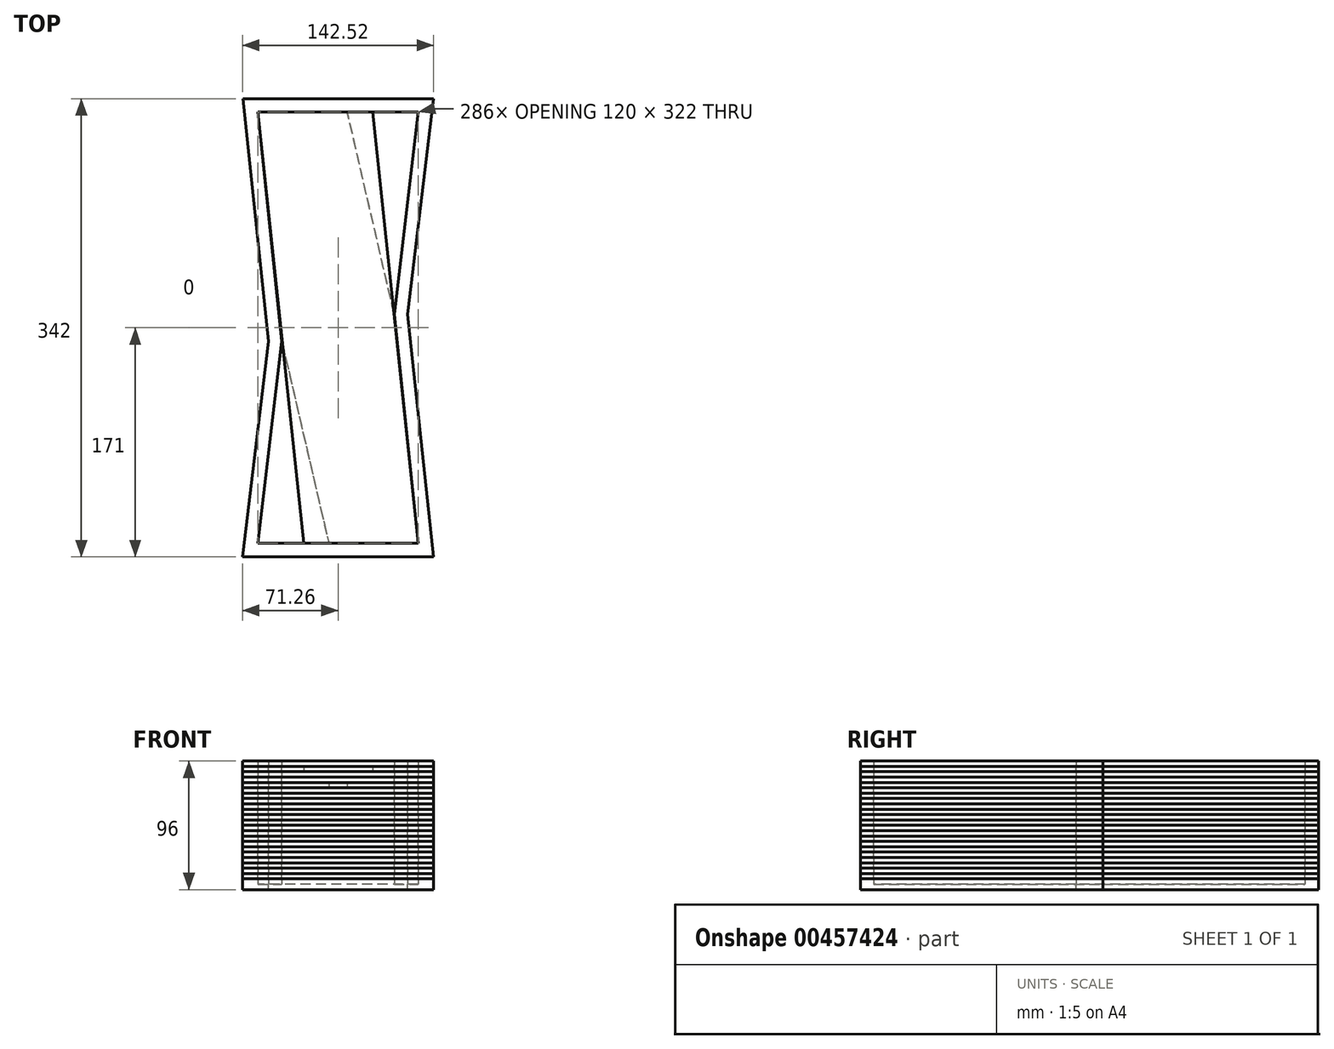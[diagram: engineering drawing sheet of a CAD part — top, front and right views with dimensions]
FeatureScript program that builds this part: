
annotation { "Feature Type Name" : "Feature", "Feature Type Description" : "" }
export const myFeature = defineFeature(function(context is Context, id is Id, definition is map)
    precondition{}
    {
        {
            var Q0;
            Q0=qCreatedBy(makeId("Top.planeOp"),FACE);
            var sketch = newSketch(context, id + "F0", { "sketchPlane" : qUnion([Q0])});
            skLineSegment(sketch, "E0", {"start": v(-71.26, -171) * mm, "end": v(-52.06, -9.93) * mm});
            skLineSegment(sketch, "E1", {"start": v(-52.06, -9.93) * mm, "end": v(-71.1, 171) * mm});
            skLineSegment(sketch, "E2", {"start": v(-71.1, 171) * mm, "end": v(71.26, 171) * mm});
            skLineSegment(sketch, "E3", {"start": v(71.26, 171) * mm, "end": v(52.06, 9.93) * mm});
            skLineSegment(sketch, "E4", {"start": v(52.06, 9.93) * mm, "end": v(71.1, -171) * mm});
            skLineSegment(sketch, "E5", {"start": v(71.1, -171) * mm, "end": v(-71.26, -171) * mm});
            skLineSegment(sketch, "E6", {"start": v(-60, 161) * mm, "end": v(-42, -10) * mm});
            skLineSegment(sketch, "E7", {"start": v(-42, -10) * mm, "end": v(-60, -161) * mm});
            skLineSegment(sketch, "E8", {"start": v(-60, -161) * mm, "end": v(60, -161) * mm});
            skLineSegment(sketch, "E9", {"start": v(60, -161) * mm, "end": v(42, 10) * mm});
            skLineSegment(sketch, "E10", {"start": v(42, 10) * mm, "end": v(60, 161) * mm});
            skLineSegment(sketch, "E11", {"start": v(60, 161) * mm, "end": v(-60, 161) * mm});
            skSolve(sketch);
        }
        {
            var Q0;
            Q0=makeQuery(id+"F0.imprint","IMPRINT",FACE,{"disambiguationData":[TD([[makeQuery(id+"F0.imprint","IMPRINT",EDGE,{"derivedFrom":sQuery(id+"F0.wireOp",EDGE,"E0")}),-1.0]])]});
            extrude(context, id + "F1", {"entities" : qUnion([Q0]), "depth" : 4 * mm});
        }
        {
            var Q0;
            Q0=makeQuery(id+"F1.opExtrude","CAP_FACE",FACE,{"disambiguationData":[OSD([sQuery(id+"F0.wireOp",EDGE,"E0"),sQuery(id+"F0.wireOp",EDGE,"E1"),sQuery(id+"F0.wireOp",EDGE,"E2"),sQuery(id+"F0.wireOp",EDGE,"E3"),sQuery(id+"F0.wireOp",EDGE,"E4"),sQuery(id+"F0.wireOp",EDGE,"E5"),sQuery(id+"F0.wireOp",EDGE,"E6"),sQuery(id+"F0.wireOp",EDGE,"E7"),sQuery(id+"F0.wireOp",EDGE,"E8"),sQuery(id+"F0.wireOp",EDGE,"E9"),sQuery(id+"F0.wireOp",EDGE,"E10"),sQuery(id+"F0.wireOp",EDGE,"E11")])],"isStart":false});
            var sketch = newSketch(context, id + "F2", { "sketchPlane" : qUnion([Q0])});
            skLineSegment(sketch, "E12", {"start": v(-71.26, -171) * mm, "end": v(-52.06, -9.93) * mm});
            skLineSegment(sketch, "E13", {"start": v(-52.06, -9.93) * mm, "end": v(-71.1, 171) * mm});
            skLineSegment(sketch, "E14", {"start": v(-71.1, 171) * mm, "end": v(71.26, 171) * mm});
            skLineSegment(sketch, "E15", {"start": v(71.26, 171) * mm, "end": v(52.06, 9.93) * mm});
            skLineSegment(sketch, "E16", {"start": v(52.06, 9.93) * mm, "end": v(71.1, -171) * mm});
            skLineSegment(sketch, "E17", {"start": v(71.1, -171) * mm, "end": v(-71.26, -171) * mm});
            skLineSegment(sketch, "E18", {"start": v(-60, 161) * mm, "end": v(-42, -10) * mm});
            skLineSegment(sketch, "E19", {"start": v(-42, -10) * mm, "end": v(-60, -161) * mm});
            skLineSegment(sketch, "E20", {"start": v(-60, -161) * mm, "end": v(60, -161) * mm});
            skLineSegment(sketch, "E21", {"start": v(60, -161) * mm, "end": v(42, 10) * mm});
            skLineSegment(sketch, "E22", {"start": v(42, 10) * mm, "end": v(60, 161) * mm});
            skLineSegment(sketch, "E23", {"start": v(60, 161) * mm, "end": v(-60, 161) * mm});
            skLineSegment(sketch, "E24", {"start": v(60, -161) * mm, "end": v(25.85, 161) * mm});
            skLineSegment(sketch, "E25", {"start": v(25.85, 161) * mm, "end": v(-60, 161) * mm});
            skLineSegment(sketch, "E26", {"start": v(-60, 161) * mm, "end": v(-25.53, -161) * mm});
            skLineSegment(sketch, "E27", {"start": v(-25.53, -161) * mm, "end": v(60, -161) * mm});
            skSolve(sketch);
        }
        {
            var Q0;
            Q0=makeQuery(id+"F2.imprint","IMPRINT",FACE,{"disambiguationData":[TD([[makeQuery(id+"F2.imprint","IMPRINT",EDGE,{"derivedFrom":sQuery(id+"F2.wireOp",EDGE,"E24")}),1.0]])]});
            extrude(context, id + "F3", {"entities" : qUnion([Q0]), "depth" : 4 * mm});
        }
        {
            var Q0;
            Q0=makeQuery(id+"F1.opExtrude","SWEPT_BODY",BODY,{"disambiguationData":[OSD([sQuery(id+"F0.wireOp",EDGE,"E0"),sQuery(id+"F0.wireOp",EDGE,"E1"),sQuery(id+"F0.wireOp",EDGE,"E2"),sQuery(id+"F0.wireOp",EDGE,"E3"),sQuery(id+"F0.wireOp",EDGE,"E4"),sQuery(id+"F0.wireOp",EDGE,"E5"),sQuery(id+"F0.wireOp",EDGE,"E6"),sQuery(id+"F0.wireOp",EDGE,"E7"),sQuery(id+"F0.wireOp",EDGE,"E8"),sQuery(id+"F0.wireOp",EDGE,"E9"),sQuery(id+"F0.wireOp",EDGE,"E10"),sQuery(id+"F0.wireOp",EDGE,"E11")])]});
            var Q1;
            Q1=makeQuery(id+"F1.opExtrude","CAP_FACE",FACE,{"disambiguationData":[OSD([sQuery(id+"F0.wireOp",EDGE,"E0"),sQuery(id+"F0.wireOp",EDGE,"E1"),sQuery(id+"F0.wireOp",EDGE,"E2"),sQuery(id+"F0.wireOp",EDGE,"E3"),sQuery(id+"F0.wireOp",EDGE,"E4"),sQuery(id+"F0.wireOp",EDGE,"E5"),sQuery(id+"F0.wireOp",EDGE,"E6"),sQuery(id+"F0.wireOp",EDGE,"E7"),sQuery(id+"F0.wireOp",EDGE,"E8"),sQuery(id+"F0.wireOp",EDGE,"E9"),sQuery(id+"F0.wireOp",EDGE,"E10"),sQuery(id+"F0.wireOp",EDGE,"E11")])],"isStart":false});
            mirror(context, id + "F4", {"entities" : qUnion([Q0]), "mirrorPlane" : qUnion([Q1])});
        }
        {
            var Q0;
            Q0=makeQuery(id+"F1.opExtrude","SWEPT_BODY",BODY,{"disambiguationData":[OSD([sQuery(id+"F0.wireOp",EDGE,"E0"),sQuery(id+"F0.wireOp",EDGE,"E1"),sQuery(id+"F0.wireOp",EDGE,"E2"),sQuery(id+"F0.wireOp",EDGE,"E3"),sQuery(id+"F0.wireOp",EDGE,"E4"),sQuery(id+"F0.wireOp",EDGE,"E5"),sQuery(id+"F0.wireOp",EDGE,"E6"),sQuery(id+"F0.wireOp",EDGE,"E7"),sQuery(id+"F0.wireOp",EDGE,"E8"),sQuery(id+"F0.wireOp",EDGE,"E9"),sQuery(id+"F0.wireOp",EDGE,"E10"),sQuery(id+"F0.wireOp",EDGE,"E11")])]});
            var Q1;
            Q1=makeQuery(id+"F1.opExtrude","CAP_FACE",FACE,{"disambiguationData":[OSD([sQuery(id+"F0.wireOp",EDGE,"E0"),sQuery(id+"F0.wireOp",EDGE,"E1"),sQuery(id+"F0.wireOp",EDGE,"E2"),sQuery(id+"F0.wireOp",EDGE,"E3"),sQuery(id+"F0.wireOp",EDGE,"E4"),sQuery(id+"F0.wireOp",EDGE,"E5"),sQuery(id+"F0.wireOp",EDGE,"E6"),sQuery(id+"F0.wireOp",EDGE,"E7"),sQuery(id+"F0.wireOp",EDGE,"E8"),sQuery(id+"F0.wireOp",EDGE,"E9"),sQuery(id+"F0.wireOp",EDGE,"E10"),sQuery(id+"F0.wireOp",EDGE,"E11")])],"isStart":true});
            mirror(context, id + "F5", {"entities" : qUnion([Q0]), "mirrorPlane" : qUnion([Q1])});
        }
        {
            var Q0;
            Q0=makeQuery(id+"F4.opPattern","COPY",BODY,{"derivedFrom":makeQuery(id+"F1.opExtrude","SWEPT_BODY",BODY,{"disambiguationData":[OSD([sQuery(id+"F0.wireOp",EDGE,"E0"),sQuery(id+"F0.wireOp",EDGE,"E1"),sQuery(id+"F0.wireOp",EDGE,"E2"),sQuery(id+"F0.wireOp",EDGE,"E3"),sQuery(id+"F0.wireOp",EDGE,"E4"),sQuery(id+"F0.wireOp",EDGE,"E5"),sQuery(id+"F0.wireOp",EDGE,"E6"),sQuery(id+"F0.wireOp",EDGE,"E7"),sQuery(id+"F0.wireOp",EDGE,"E8"),sQuery(id+"F0.wireOp",EDGE,"E9"),sQuery(id+"F0.wireOp",EDGE,"E10"),sQuery(id+"F0.wireOp",EDGE,"E11")])]}),"instanceName":"1"});
            var Q1;
            Q1=makeQuery(id+"F4.opPattern","COPY",FACE,{"derivedFrom":makeQuery(id+"F1.opExtrude","CAP_FACE",FACE,{"disambiguationData":[OSD([sQuery(id+"F0.wireOp",EDGE,"E0"),sQuery(id+"F0.wireOp",EDGE,"E1"),sQuery(id+"F0.wireOp",EDGE,"E2"),sQuery(id+"F0.wireOp",EDGE,"E3"),sQuery(id+"F0.wireOp",EDGE,"E4"),sQuery(id+"F0.wireOp",EDGE,"E5"),sQuery(id+"F0.wireOp",EDGE,"E6"),sQuery(id+"F0.wireOp",EDGE,"E7"),sQuery(id+"F0.wireOp",EDGE,"E8"),sQuery(id+"F0.wireOp",EDGE,"E9"),sQuery(id+"F0.wireOp",EDGE,"E10"),sQuery(id+"F0.wireOp",EDGE,"E11")])],"isStart":true}),"instanceName":"1"});
            mirror(context, id + "F6", {"entities" : qUnion([Q0]), "mirrorPlane" : qUnion([Q1])});
        }
        {
            var Q0;
            Q0=makeQuery(id+"F5.opPattern","COPY",FACE,{"derivedFrom":makeQuery(id+"F1.opExtrude","CAP_FACE",FACE,{"disambiguationData":[OSD([sQuery(id+"F0.wireOp",EDGE,"E0"),sQuery(id+"F0.wireOp",EDGE,"E1"),sQuery(id+"F0.wireOp",EDGE,"E2"),sQuery(id+"F0.wireOp",EDGE,"E3"),sQuery(id+"F0.wireOp",EDGE,"E4"),sQuery(id+"F0.wireOp",EDGE,"E5"),sQuery(id+"F0.wireOp",EDGE,"E6"),sQuery(id+"F0.wireOp",EDGE,"E7"),sQuery(id+"F0.wireOp",EDGE,"E8"),sQuery(id+"F0.wireOp",EDGE,"E9"),sQuery(id+"F0.wireOp",EDGE,"E10"),sQuery(id+"F0.wireOp",EDGE,"E11")])],"isStart":false}),"instanceName":"1"});
            var sketch = newSketch(context, id + "F7", { "sketchPlane" : qUnion([Q0])});
            skLineSegment(sketch, "E28", {"start": v(71.26, -171) * mm, "end": v(52.06, -9.93) * mm});
            skLineSegment(sketch, "E29", {"start": v(52.06, -9.93) * mm, "end": v(71.1, 171) * mm});
            skLineSegment(sketch, "E30", {"start": v(71.1, 171) * mm, "end": v(-71.26, 171) * mm});
            skLineSegment(sketch, "E31", {"start": v(-71.26, 171) * mm, "end": v(-52.06, 9.93) * mm});
            skLineSegment(sketch, "E32", {"start": v(-52.06, 9.93) * mm, "end": v(-71.1, -171) * mm});
            skLineSegment(sketch, "E33", {"start": v(-71.1, -171) * mm, "end": v(71.26, -171) * mm});
            skLineSegment(sketch, "E34", {"start": v(60, 161) * mm, "end": v(42, -10) * mm});
            skLineSegment(sketch, "E35", {"start": v(42, -10) * mm, "end": v(60, -161) * mm});
            skLineSegment(sketch, "E36", {"start": v(60, -161) * mm, "end": v(-60, -161) * mm});
            skLineSegment(sketch, "E37", {"start": v(-60, -161) * mm, "end": v(-42, 10) * mm});
            skLineSegment(sketch, "E38", {"start": v(-42, 10) * mm, "end": v(-60, 161) * mm});
            skLineSegment(sketch, "E39", {"start": v(-60, 161) * mm, "end": v(60, 161) * mm});
            skLineSegment(sketch, "E40", {"start": v(-42, 10) * mm, "end": v(-6.94, 161) * mm});
            skLineSegment(sketch, "E41", {"start": v(-6.94, 161) * mm, "end": v(-60, 161) * mm});
            skLineSegment(sketch, "E42", {"start": v(-60, 161) * mm, "end": v(-42, 10) * mm});
            skLineSegment(sketch, "E43", {"start": v(42, -10) * mm, "end": v(6.94, -161) * mm});
            skLineSegment(sketch, "E44", {"start": v(6.94, -161) * mm, "end": v(60, -161) * mm});
            skLineSegment(sketch, "E45", {"start": v(60, -161) * mm, "end": v(42, -10) * mm});
            skSolve(sketch);
        }
        {
            var Q0;
            Q0=makeQuery(id+"F7.imprint","IMPRINT",FACE,{"disambiguationData":[TD([[makeQuery(id+"F7.imprint","IMPRINT",EDGE,{"derivedFrom":sQuery(id+"F7.wireOp",EDGE,"E43")}),1.0]])]});
            var Q1;
            {var subQ1=makeQuery(id+"F5.opPattern","COPY",EDGE,{"derivedFrom":makeQuery(id+"F1.opExtrude","CAP_EDGE",EDGE,{"disambiguationData":[OSD([sQuery(id+"F0.wireOp",EDGE,"E8")])],"isStart":false}),"instanceName":"1"});var subQ3=makeQuery(id+"F5.opPattern","COPY",EDGE,{"derivedFrom":makeQuery(id+"F1.opExtrude","CAP_EDGE",EDGE,{"disambiguationData":[OSD([sQuery(id+"F0.wireOp",EDGE,"E7")])],"isStart":false}),"instanceName":"1"});var subQ5=makeQuery(id+"F7.imprint","INTERSECT",VERTEX,{"derivedFrom":[subQ3,subQ1]});Q1=makeQuery(id+"F7.imprint","IMPRINT",FACE,{"disambiguationData":[TD([[makeQuery(id+"F7.imprint","IMPRINT",EDGE,{"disambiguationData":[TD([[subQ5,1.0]])],"derivedFrom":subQ3}),-1.0]])]});}
            extrude(context, id + "F8", {"entities" : qUnion([Q0, Q1]), "depth" : 4 * mm});
        }
        {
            var Q0;
            Q0=makeQuery(id+"F6.opPattern","COPY",BODY,{"derivedFrom":makeQuery(id+"F4.opPattern","COPY",BODY,{"derivedFrom":makeQuery(id+"F1.opExtrude","SWEPT_BODY",BODY,{"disambiguationData":[OSD([sQuery(id+"F0.wireOp",EDGE,"E0"),sQuery(id+"F0.wireOp",EDGE,"E1"),sQuery(id+"F0.wireOp",EDGE,"E2"),sQuery(id+"F0.wireOp",EDGE,"E3"),sQuery(id+"F0.wireOp",EDGE,"E4"),sQuery(id+"F0.wireOp",EDGE,"E5"),sQuery(id+"F0.wireOp",EDGE,"E6"),sQuery(id+"F0.wireOp",EDGE,"E7"),sQuery(id+"F0.wireOp",EDGE,"E8"),sQuery(id+"F0.wireOp",EDGE,"E9"),sQuery(id+"F0.wireOp",EDGE,"E10"),sQuery(id+"F0.wireOp",EDGE,"E11")])]}),"instanceName":"1"}),"instanceName":"1"});
            var Q1;
            Q1=makeQuery(id+"F4.opPattern","COPY",BODY,{"derivedFrom":makeQuery(id+"F1.opExtrude","SWEPT_BODY",BODY,{"disambiguationData":[OSD([sQuery(id+"F0.wireOp",EDGE,"E0"),sQuery(id+"F0.wireOp",EDGE,"E1"),sQuery(id+"F0.wireOp",EDGE,"E2"),sQuery(id+"F0.wireOp",EDGE,"E3"),sQuery(id+"F0.wireOp",EDGE,"E4"),sQuery(id+"F0.wireOp",EDGE,"E5"),sQuery(id+"F0.wireOp",EDGE,"E6"),sQuery(id+"F0.wireOp",EDGE,"E7"),sQuery(id+"F0.wireOp",EDGE,"E8"),sQuery(id+"F0.wireOp",EDGE,"E9"),sQuery(id+"F0.wireOp",EDGE,"E10"),sQuery(id+"F0.wireOp",EDGE,"E11")])]}),"instanceName":"1"});
            var Q2;
            Q2=makeQuery(id+"F1.opExtrude","SWEPT_BODY",BODY,{"disambiguationData":[OSD([sQuery(id+"F0.wireOp",EDGE,"E0"),sQuery(id+"F0.wireOp",EDGE,"E1"),sQuery(id+"F0.wireOp",EDGE,"E2"),sQuery(id+"F0.wireOp",EDGE,"E3"),sQuery(id+"F0.wireOp",EDGE,"E4"),sQuery(id+"F0.wireOp",EDGE,"E5"),sQuery(id+"F0.wireOp",EDGE,"E6"),sQuery(id+"F0.wireOp",EDGE,"E7"),sQuery(id+"F0.wireOp",EDGE,"E8"),sQuery(id+"F0.wireOp",EDGE,"E9"),sQuery(id+"F0.wireOp",EDGE,"E10"),sQuery(id+"F0.wireOp",EDGE,"E11")])]});
            var Q3;
            Q3=makeQuery(id+"F5.opPattern","COPY",BODY,{"derivedFrom":makeQuery(id+"F1.opExtrude","SWEPT_BODY",BODY,{"disambiguationData":[OSD([sQuery(id+"F0.wireOp",EDGE,"E0"),sQuery(id+"F0.wireOp",EDGE,"E1"),sQuery(id+"F0.wireOp",EDGE,"E2"),sQuery(id+"F0.wireOp",EDGE,"E3"),sQuery(id+"F0.wireOp",EDGE,"E4"),sQuery(id+"F0.wireOp",EDGE,"E5"),sQuery(id+"F0.wireOp",EDGE,"E6"),sQuery(id+"F0.wireOp",EDGE,"E7"),sQuery(id+"F0.wireOp",EDGE,"E8"),sQuery(id+"F0.wireOp",EDGE,"E9"),sQuery(id+"F0.wireOp",EDGE,"E10"),sQuery(id+"F0.wireOp",EDGE,"E11")])]}),"instanceName":"1"});
            var Q4;
            Q4=makeQuery(id+"F5.opPattern","COPY",FACE,{"derivedFrom":makeQuery(id+"F1.opExtrude","CAP_FACE",FACE,{"disambiguationData":[OSD([sQuery(id+"F0.wireOp",EDGE,"E0"),sQuery(id+"F0.wireOp",EDGE,"E1"),sQuery(id+"F0.wireOp",EDGE,"E2"),sQuery(id+"F0.wireOp",EDGE,"E3"),sQuery(id+"F0.wireOp",EDGE,"E4"),sQuery(id+"F0.wireOp",EDGE,"E5"),sQuery(id+"F0.wireOp",EDGE,"E6"),sQuery(id+"F0.wireOp",EDGE,"E7"),sQuery(id+"F0.wireOp",EDGE,"E8"),sQuery(id+"F0.wireOp",EDGE,"E9"),sQuery(id+"F0.wireOp",EDGE,"E10"),sQuery(id+"F0.wireOp",EDGE,"E11")])],"isStart":false}),"instanceName":"1"});
            mirror(context, id + "F9", {"entities" : qUnion([Q0, Q1, Q2, Q3]), "mirrorPlane" : qUnion([Q4])});
        }
        {
            var Q0;
            Q0=makeQuery(id+"F6.opPattern","COPY",BODY,{"derivedFrom":makeQuery(id+"F4.opPattern","COPY",BODY,{"derivedFrom":makeQuery(id+"F1.opExtrude","SWEPT_BODY",BODY,{"disambiguationData":[OSD([sQuery(id+"F0.wireOp",EDGE,"E0"),sQuery(id+"F0.wireOp",EDGE,"E1"),sQuery(id+"F0.wireOp",EDGE,"E2"),sQuery(id+"F0.wireOp",EDGE,"E3"),sQuery(id+"F0.wireOp",EDGE,"E4"),sQuery(id+"F0.wireOp",EDGE,"E5"),sQuery(id+"F0.wireOp",EDGE,"E6"),sQuery(id+"F0.wireOp",EDGE,"E7"),sQuery(id+"F0.wireOp",EDGE,"E8"),sQuery(id+"F0.wireOp",EDGE,"E9"),sQuery(id+"F0.wireOp",EDGE,"E10"),sQuery(id+"F0.wireOp",EDGE,"E11")])]}),"instanceName":"1"}),"instanceName":"1"});
            var Q1;
            Q1=makeQuery(id+"F4.opPattern","COPY",BODY,{"derivedFrom":makeQuery(id+"F1.opExtrude","SWEPT_BODY",BODY,{"disambiguationData":[OSD([sQuery(id+"F0.wireOp",EDGE,"E0"),sQuery(id+"F0.wireOp",EDGE,"E1"),sQuery(id+"F0.wireOp",EDGE,"E2"),sQuery(id+"F0.wireOp",EDGE,"E3"),sQuery(id+"F0.wireOp",EDGE,"E4"),sQuery(id+"F0.wireOp",EDGE,"E5"),sQuery(id+"F0.wireOp",EDGE,"E6"),sQuery(id+"F0.wireOp",EDGE,"E7"),sQuery(id+"F0.wireOp",EDGE,"E8"),sQuery(id+"F0.wireOp",EDGE,"E9"),sQuery(id+"F0.wireOp",EDGE,"E10"),sQuery(id+"F0.wireOp",EDGE,"E11")])]}),"instanceName":"1"});
            var Q2;
            Q2=makeQuery(id+"F1.opExtrude","SWEPT_BODY",BODY,{"disambiguationData":[OSD([sQuery(id+"F0.wireOp",EDGE,"E0"),sQuery(id+"F0.wireOp",EDGE,"E1"),sQuery(id+"F0.wireOp",EDGE,"E2"),sQuery(id+"F0.wireOp",EDGE,"E3"),sQuery(id+"F0.wireOp",EDGE,"E4"),sQuery(id+"F0.wireOp",EDGE,"E5"),sQuery(id+"F0.wireOp",EDGE,"E6"),sQuery(id+"F0.wireOp",EDGE,"E7"),sQuery(id+"F0.wireOp",EDGE,"E8"),sQuery(id+"F0.wireOp",EDGE,"E9"),sQuery(id+"F0.wireOp",EDGE,"E10"),sQuery(id+"F0.wireOp",EDGE,"E11")])]});
            var Q3;
            Q3=makeQuery(id+"F5.opPattern","COPY",BODY,{"derivedFrom":makeQuery(id+"F1.opExtrude","SWEPT_BODY",BODY,{"disambiguationData":[OSD([sQuery(id+"F0.wireOp",EDGE,"E0"),sQuery(id+"F0.wireOp",EDGE,"E1"),sQuery(id+"F0.wireOp",EDGE,"E2"),sQuery(id+"F0.wireOp",EDGE,"E3"),sQuery(id+"F0.wireOp",EDGE,"E4"),sQuery(id+"F0.wireOp",EDGE,"E5"),sQuery(id+"F0.wireOp",EDGE,"E6"),sQuery(id+"F0.wireOp",EDGE,"E7"),sQuery(id+"F0.wireOp",EDGE,"E8"),sQuery(id+"F0.wireOp",EDGE,"E9"),sQuery(id+"F0.wireOp",EDGE,"E10"),sQuery(id+"F0.wireOp",EDGE,"E11")])]}),"instanceName":"1"});
            var Q4;
            Q4=makeQuery(id+"F9.opPattern","COPY",BODY,{"derivedFrom":makeQuery(id+"F5.opPattern","COPY",BODY,{"derivedFrom":makeQuery(id+"F1.opExtrude","SWEPT_BODY",BODY,{"disambiguationData":[OSD([sQuery(id+"F0.wireOp",EDGE,"E0"),sQuery(id+"F0.wireOp",EDGE,"E1"),sQuery(id+"F0.wireOp",EDGE,"E2"),sQuery(id+"F0.wireOp",EDGE,"E3"),sQuery(id+"F0.wireOp",EDGE,"E4"),sQuery(id+"F0.wireOp",EDGE,"E5"),sQuery(id+"F0.wireOp",EDGE,"E6"),sQuery(id+"F0.wireOp",EDGE,"E7"),sQuery(id+"F0.wireOp",EDGE,"E8"),sQuery(id+"F0.wireOp",EDGE,"E9"),sQuery(id+"F0.wireOp",EDGE,"E10"),sQuery(id+"F0.wireOp",EDGE,"E11")])]}),"instanceName":"1"}),"instanceName":"1"});
            var Q5;
            Q5=makeQuery(id+"F9.opPattern","COPY",BODY,{"derivedFrom":makeQuery(id+"F1.opExtrude","SWEPT_BODY",BODY,{"disambiguationData":[OSD([sQuery(id+"F0.wireOp",EDGE,"E0"),sQuery(id+"F0.wireOp",EDGE,"E1"),sQuery(id+"F0.wireOp",EDGE,"E2"),sQuery(id+"F0.wireOp",EDGE,"E3"),sQuery(id+"F0.wireOp",EDGE,"E4"),sQuery(id+"F0.wireOp",EDGE,"E5"),sQuery(id+"F0.wireOp",EDGE,"E6"),sQuery(id+"F0.wireOp",EDGE,"E7"),sQuery(id+"F0.wireOp",EDGE,"E8"),sQuery(id+"F0.wireOp",EDGE,"E9"),sQuery(id+"F0.wireOp",EDGE,"E10"),sQuery(id+"F0.wireOp",EDGE,"E11")])]}),"instanceName":"1"});
            var Q6;
            Q6=makeQuery(id+"F9.opPattern","COPY",BODY,{"derivedFrom":makeQuery(id+"F4.opPattern","COPY",BODY,{"derivedFrom":makeQuery(id+"F1.opExtrude","SWEPT_BODY",BODY,{"disambiguationData":[OSD([sQuery(id+"F0.wireOp",EDGE,"E0"),sQuery(id+"F0.wireOp",EDGE,"E1"),sQuery(id+"F0.wireOp",EDGE,"E2"),sQuery(id+"F0.wireOp",EDGE,"E3"),sQuery(id+"F0.wireOp",EDGE,"E4"),sQuery(id+"F0.wireOp",EDGE,"E5"),sQuery(id+"F0.wireOp",EDGE,"E6"),sQuery(id+"F0.wireOp",EDGE,"E7"),sQuery(id+"F0.wireOp",EDGE,"E8"),sQuery(id+"F0.wireOp",EDGE,"E9"),sQuery(id+"F0.wireOp",EDGE,"E10"),sQuery(id+"F0.wireOp",EDGE,"E11")])]}),"instanceName":"1"}),"instanceName":"1"});
            var Q7;
            Q7=makeQuery(id+"F9.opPattern","COPY",BODY,{"derivedFrom":makeQuery(id+"F6.opPattern","COPY",BODY,{"derivedFrom":makeQuery(id+"F4.opPattern","COPY",BODY,{"derivedFrom":makeQuery(id+"F1.opExtrude","SWEPT_BODY",BODY,{"disambiguationData":[OSD([sQuery(id+"F0.wireOp",EDGE,"E0"),sQuery(id+"F0.wireOp",EDGE,"E1"),sQuery(id+"F0.wireOp",EDGE,"E2"),sQuery(id+"F0.wireOp",EDGE,"E3"),sQuery(id+"F0.wireOp",EDGE,"E4"),sQuery(id+"F0.wireOp",EDGE,"E5"),sQuery(id+"F0.wireOp",EDGE,"E6"),sQuery(id+"F0.wireOp",EDGE,"E7"),sQuery(id+"F0.wireOp",EDGE,"E8"),sQuery(id+"F0.wireOp",EDGE,"E9"),sQuery(id+"F0.wireOp",EDGE,"E10"),sQuery(id+"F0.wireOp",EDGE,"E11")])]}),"instanceName":"1"}),"instanceName":"1"}),"instanceName":"1"});
            var Q8;
            Q8=makeQuery(id+"F9.opPattern","COPY",FACE,{"derivedFrom":makeQuery(id+"F6.opPattern","COPY",FACE,{"derivedFrom":makeQuery(id+"F4.opPattern","COPY",FACE,{"derivedFrom":makeQuery(id+"F1.opExtrude","CAP_FACE",FACE,{"disambiguationData":[OSD([sQuery(id+"F0.wireOp",EDGE,"E0"),sQuery(id+"F0.wireOp",EDGE,"E1"),sQuery(id+"F0.wireOp",EDGE,"E2"),sQuery(id+"F0.wireOp",EDGE,"E3"),sQuery(id+"F0.wireOp",EDGE,"E4"),sQuery(id+"F0.wireOp",EDGE,"E5"),sQuery(id+"F0.wireOp",EDGE,"E6"),sQuery(id+"F0.wireOp",EDGE,"E7"),sQuery(id+"F0.wireOp",EDGE,"E8"),sQuery(id+"F0.wireOp",EDGE,"E9"),sQuery(id+"F0.wireOp",EDGE,"E10"),sQuery(id+"F0.wireOp",EDGE,"E11")])],"isStart":false}),"instanceName":"1"}),"instanceName":"1"}),"instanceName":"1"});
            mirror(context, id + "F10", {"entities" : qUnion([Q0, Q1, Q2, Q3, Q4, Q5, Q6, Q7]), "mirrorPlane" : qUnion([Q8])});
        }
        {
            var Q0;
            Q0=makeQuery(id+"F10.opPattern","COPY",BODY,{"derivedFrom":makeQuery(id+"F6.opPattern","COPY",BODY,{"derivedFrom":makeQuery(id+"F4.opPattern","COPY",BODY,{"derivedFrom":makeQuery(id+"F1.opExtrude","SWEPT_BODY",BODY,{"disambiguationData":[OSD([sQuery(id+"F0.wireOp",EDGE,"E0"),sQuery(id+"F0.wireOp",EDGE,"E1"),sQuery(id+"F0.wireOp",EDGE,"E2"),sQuery(id+"F0.wireOp",EDGE,"E3"),sQuery(id+"F0.wireOp",EDGE,"E4"),sQuery(id+"F0.wireOp",EDGE,"E5"),sQuery(id+"F0.wireOp",EDGE,"E6"),sQuery(id+"F0.wireOp",EDGE,"E7"),sQuery(id+"F0.wireOp",EDGE,"E8"),sQuery(id+"F0.wireOp",EDGE,"E9"),sQuery(id+"F0.wireOp",EDGE,"E10"),sQuery(id+"F0.wireOp",EDGE,"E11")])]}),"instanceName":"1"}),"instanceName":"1"}),"instanceName":"1"});
            var Q1;
            Q1=makeQuery(id+"F10.opPattern","COPY",BODY,{"derivedFrom":makeQuery(id+"F4.opPattern","COPY",BODY,{"derivedFrom":makeQuery(id+"F1.opExtrude","SWEPT_BODY",BODY,{"disambiguationData":[OSD([sQuery(id+"F0.wireOp",EDGE,"E0"),sQuery(id+"F0.wireOp",EDGE,"E1"),sQuery(id+"F0.wireOp",EDGE,"E2"),sQuery(id+"F0.wireOp",EDGE,"E3"),sQuery(id+"F0.wireOp",EDGE,"E4"),sQuery(id+"F0.wireOp",EDGE,"E5"),sQuery(id+"F0.wireOp",EDGE,"E6"),sQuery(id+"F0.wireOp",EDGE,"E7"),sQuery(id+"F0.wireOp",EDGE,"E8"),sQuery(id+"F0.wireOp",EDGE,"E9"),sQuery(id+"F0.wireOp",EDGE,"E10"),sQuery(id+"F0.wireOp",EDGE,"E11")])]}),"instanceName":"1"}),"instanceName":"1"});
            var Q2;
            Q2=makeQuery(id+"F10.opPattern","COPY",BODY,{"derivedFrom":makeQuery(id+"F1.opExtrude","SWEPT_BODY",BODY,{"disambiguationData":[OSD([sQuery(id+"F0.wireOp",EDGE,"E0"),sQuery(id+"F0.wireOp",EDGE,"E1"),sQuery(id+"F0.wireOp",EDGE,"E2"),sQuery(id+"F0.wireOp",EDGE,"E3"),sQuery(id+"F0.wireOp",EDGE,"E4"),sQuery(id+"F0.wireOp",EDGE,"E5"),sQuery(id+"F0.wireOp",EDGE,"E6"),sQuery(id+"F0.wireOp",EDGE,"E7"),sQuery(id+"F0.wireOp",EDGE,"E8"),sQuery(id+"F0.wireOp",EDGE,"E9"),sQuery(id+"F0.wireOp",EDGE,"E10"),sQuery(id+"F0.wireOp",EDGE,"E11")])]}),"instanceName":"1"});
            var Q3;
            Q3=makeQuery(id+"F10.opPattern","COPY",BODY,{"derivedFrom":makeQuery(id+"F5.opPattern","COPY",BODY,{"derivedFrom":makeQuery(id+"F1.opExtrude","SWEPT_BODY",BODY,{"disambiguationData":[OSD([sQuery(id+"F0.wireOp",EDGE,"E0"),sQuery(id+"F0.wireOp",EDGE,"E1"),sQuery(id+"F0.wireOp",EDGE,"E2"),sQuery(id+"F0.wireOp",EDGE,"E3"),sQuery(id+"F0.wireOp",EDGE,"E4"),sQuery(id+"F0.wireOp",EDGE,"E5"),sQuery(id+"F0.wireOp",EDGE,"E6"),sQuery(id+"F0.wireOp",EDGE,"E7"),sQuery(id+"F0.wireOp",EDGE,"E8"),sQuery(id+"F0.wireOp",EDGE,"E9"),sQuery(id+"F0.wireOp",EDGE,"E10"),sQuery(id+"F0.wireOp",EDGE,"E11")])]}),"instanceName":"1"}),"instanceName":"1"});
            var Q4;
            Q4=makeQuery(id+"F10.opPattern","COPY",BODY,{"derivedFrom":makeQuery(id+"F9.opPattern","COPY",BODY,{"derivedFrom":makeQuery(id+"F5.opPattern","COPY",BODY,{"derivedFrom":makeQuery(id+"F1.opExtrude","SWEPT_BODY",BODY,{"disambiguationData":[OSD([sQuery(id+"F0.wireOp",EDGE,"E0"),sQuery(id+"F0.wireOp",EDGE,"E1"),sQuery(id+"F0.wireOp",EDGE,"E2"),sQuery(id+"F0.wireOp",EDGE,"E3"),sQuery(id+"F0.wireOp",EDGE,"E4"),sQuery(id+"F0.wireOp",EDGE,"E5"),sQuery(id+"F0.wireOp",EDGE,"E6"),sQuery(id+"F0.wireOp",EDGE,"E7"),sQuery(id+"F0.wireOp",EDGE,"E8"),sQuery(id+"F0.wireOp",EDGE,"E9"),sQuery(id+"F0.wireOp",EDGE,"E10"),sQuery(id+"F0.wireOp",EDGE,"E11")])]}),"instanceName":"1"}),"instanceName":"1"}),"instanceName":"1"});
            var Q5;
            Q5=makeQuery(id+"F10.opPattern","COPY",BODY,{"derivedFrom":makeQuery(id+"F9.opPattern","COPY",BODY,{"derivedFrom":makeQuery(id+"F1.opExtrude","SWEPT_BODY",BODY,{"disambiguationData":[OSD([sQuery(id+"F0.wireOp",EDGE,"E0"),sQuery(id+"F0.wireOp",EDGE,"E1"),sQuery(id+"F0.wireOp",EDGE,"E2"),sQuery(id+"F0.wireOp",EDGE,"E3"),sQuery(id+"F0.wireOp",EDGE,"E4"),sQuery(id+"F0.wireOp",EDGE,"E5"),sQuery(id+"F0.wireOp",EDGE,"E6"),sQuery(id+"F0.wireOp",EDGE,"E7"),sQuery(id+"F0.wireOp",EDGE,"E8"),sQuery(id+"F0.wireOp",EDGE,"E9"),sQuery(id+"F0.wireOp",EDGE,"E10"),sQuery(id+"F0.wireOp",EDGE,"E11")])]}),"instanceName":"1"}),"instanceName":"1"});
            var Q6;
            Q6=makeQuery(id+"F10.opPattern","COPY",BODY,{"derivedFrom":makeQuery(id+"F9.opPattern","COPY",BODY,{"derivedFrom":makeQuery(id+"F4.opPattern","COPY",BODY,{"derivedFrom":makeQuery(id+"F1.opExtrude","SWEPT_BODY",BODY,{"disambiguationData":[OSD([sQuery(id+"F0.wireOp",EDGE,"E0"),sQuery(id+"F0.wireOp",EDGE,"E1"),sQuery(id+"F0.wireOp",EDGE,"E2"),sQuery(id+"F0.wireOp",EDGE,"E3"),sQuery(id+"F0.wireOp",EDGE,"E4"),sQuery(id+"F0.wireOp",EDGE,"E5"),sQuery(id+"F0.wireOp",EDGE,"E6"),sQuery(id+"F0.wireOp",EDGE,"E7"),sQuery(id+"F0.wireOp",EDGE,"E8"),sQuery(id+"F0.wireOp",EDGE,"E9"),sQuery(id+"F0.wireOp",EDGE,"E10"),sQuery(id+"F0.wireOp",EDGE,"E11")])]}),"instanceName":"1"}),"instanceName":"1"}),"instanceName":"1"});
            var Q7;
            Q7=makeQuery(id+"F10.opPattern","COPY",FACE,{"derivedFrom":makeQuery(id+"F6.opPattern","COPY",FACE,{"derivedFrom":makeQuery(id+"F4.opPattern","COPY",FACE,{"derivedFrom":makeQuery(id+"F1.opExtrude","CAP_FACE",FACE,{"disambiguationData":[OSD([sQuery(id+"F0.wireOp",EDGE,"E0"),sQuery(id+"F0.wireOp",EDGE,"E1"),sQuery(id+"F0.wireOp",EDGE,"E2"),sQuery(id+"F0.wireOp",EDGE,"E3"),sQuery(id+"F0.wireOp",EDGE,"E4"),sQuery(id+"F0.wireOp",EDGE,"E5"),sQuery(id+"F0.wireOp",EDGE,"E6"),sQuery(id+"F0.wireOp",EDGE,"E7"),sQuery(id+"F0.wireOp",EDGE,"E8"),sQuery(id+"F0.wireOp",EDGE,"E9"),sQuery(id+"F0.wireOp",EDGE,"E10"),sQuery(id+"F0.wireOp",EDGE,"E11")])],"isStart":false}),"instanceName":"1"}),"instanceName":"1"}),"instanceName":"1"});
            mirror(context, id + "F11", {"entities" : qUnion([Q0, Q1, Q2, Q3, Q4, Q5, Q6]), "mirrorPlane" : qUnion([Q7])});
        }
        {
            var Q0;
            Q0=makeQuery(id+"F11.opPattern","COPY",FACE,{"derivedFrom":makeQuery(id+"F10.opPattern","COPY",FACE,{"derivedFrom":makeQuery(id+"F9.opPattern","COPY",FACE,{"derivedFrom":makeQuery(id+"F4.opPattern","COPY",FACE,{"derivedFrom":makeQuery(id+"F1.opExtrude","CAP_FACE",FACE,{"disambiguationData":[OSD([sQuery(id+"F0.wireOp",EDGE,"E0"),sQuery(id+"F0.wireOp",EDGE,"E1"),sQuery(id+"F0.wireOp",EDGE,"E2"),sQuery(id+"F0.wireOp",EDGE,"E3"),sQuery(id+"F0.wireOp",EDGE,"E4"),sQuery(id+"F0.wireOp",EDGE,"E5"),sQuery(id+"F0.wireOp",EDGE,"E6"),sQuery(id+"F0.wireOp",EDGE,"E7"),sQuery(id+"F0.wireOp",EDGE,"E8"),sQuery(id+"F0.wireOp",EDGE,"E9"),sQuery(id+"F0.wireOp",EDGE,"E10"),sQuery(id+"F0.wireOp",EDGE,"E11")])],"isStart":true}),"instanceName":"1"}),"instanceName":"1"}),"instanceName":"1"}),"instanceName":"1"});
            var sketch = newSketch(context, id + "F12", { "sketchPlane" : qUnion([Q0])});
            skLineSegment(sketch, "E46", {"start": v(71.26, -171) * mm, "end": v(52.06, -9.93) * mm});
            skLineSegment(sketch, "E47", {"start": v(52.06, -9.93) * mm, "end": v(71.1, 171) * mm});
            skLineSegment(sketch, "E48", {"start": v(71.1, 171) * mm, "end": v(-71.26, 171) * mm});
            skLineSegment(sketch, "E49", {"start": v(-71.26, 171) * mm, "end": v(-52.06, 9.93) * mm});
            skLineSegment(sketch, "E50", {"start": v(-52.06, 9.93) * mm, "end": v(-71.1, -171) * mm});
            skLineSegment(sketch, "E51", {"start": v(-71.1, -171) * mm, "end": v(71.26, -171) * mm});
            skSolve(sketch);
        }
        {
            var Q0;
            Q0 = qSketchRegion(id + "F12", true);
            extrude(context, id + "F13", {"entities" : qUnion([Q0]), "operationType" : NewBodyOperationType.ADD, "depth" : 4 * mm});
        }
    });
